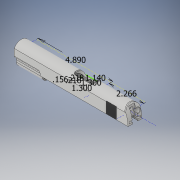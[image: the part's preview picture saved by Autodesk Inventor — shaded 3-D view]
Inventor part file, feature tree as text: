
AUTODESK INVENTOR PART (.ipt)
format: ipt  version: 2018.3 (Build 223284000, 284)  size: 577,536 bytes
history: native  units: in
note: dims shown in document units (in); Inventor stores cm internally (conversion verified against a paired STEP export)
features: extrude x11, sketch x10, plane x2, fillet x2, revolve x2, chamfer x2
ambient origin geometry x8: Origin, YZ Plane, XZ Plane, XY Plane, X Axis, Y Axis, Z Axis, Center Point
bodies: Solid1 (feature_tree)
feature tree (29):
  sketch  "Sketch1"  dims[d0=0.499in d1=0.635in]
  extrude  "Extrusion1"  Depth=0.635in
  sketch  "Sketch2"  dims[d2=0.64in d3=0.496in]
  extrude  "Extrusion2"  Depth=0.496in
  extrude  "Extrusion3"  Depth=0.183in
  extrude  "Extrusion4"  Depth=0.98in
  sketch  "Sketch4"  dims[d6=0.699in d7=0.98in]
  plane  "Work Plane1"
  extrude  "Extrusion5"  Depth=0.234in
  fillet  "Fillet1"  Radius=0.916in
  revolve  "Revolution1"  [1 undecoded]
  revolve  "Revolution2"  [1 undecoded]
  extrude  "Extrusion6"  Depth=5.958in TaperAngle=0.0deg
  extrude  "Extrusion7"  Depth=1.698in
  fillet  "Fillet2"  Radius=3.834in
  extrude  "Extrusion8"  Depth=0.3125in
  sketch  "Sketch9"  dims[d21=7.656in d22=0.0in d23=1.698in d24=3.834in]
  plane  "Work Plane2"
  extrude  "Extrusion9"  Depth=0.3125in
  chamfer  "Chamfer1"  Distance=0.218in
  chamfer  "Chamfer2"  Distance=1.3in
  extrude  "Extrusion10"  Depth=0.3125in
  extrude  "Extrusion11"  Depth=0.3125in
  sketch  "Sketch3"  dims[d4=0.183in d5=0.183in]
  sketch  "Sketch5"  dims[d9=0.234in d10=0.234in d11=0.916in]
  sketch  "Sketch6"  dims[d12=0.5033in d13=7.656in d14=0.0in]
  sketch  "Sketch7"  dims[d15=1.698in d16=0.496in]
  sketch  "Sketch8"  dims[d17=7.656in d18=0.0in d19=5.958in d20=0.0in]
  sketch  "Sketch10"  dims[d27=4.89in d28=2.266in d29=1.3in d30=0.218in d31=1.3in d32=0.218in d33=1.14in d34=0.156in d35=0.1in d36=7.656in d37=0.0in d38=0.3125in d39=7.156in d40=1.818in d41=90.0deg d46=90.0deg d47=7.656in d48=0.0in d49=7.656in d50=0.0in d51=0.118in d52=0.496in d53=0.101in d54=0.377in d55=0.377in d56=7.656in d57=0.078in d58=0.0in d59=0.0in d60=0.1in d61=0.2686in d62=0.409in d64=0.2725in d65=0.0in d66=7.656in d67=2.328in d68=0.0in d69=0.0in d70=0.0625in d71=0.125in d72=45.0deg d73=0.02in d74=0.125in d75=45.0deg d76=0.02in d77=0.02in d78=60.0deg d79=7.656in d80=0.0in d81=4.906in d82=0.0in]
note: 2 required parameter values undecoded (feature->parameter linkage not recoverable at this tier; creation-order binding heuristic only, values carry confidence <= 0.55)
